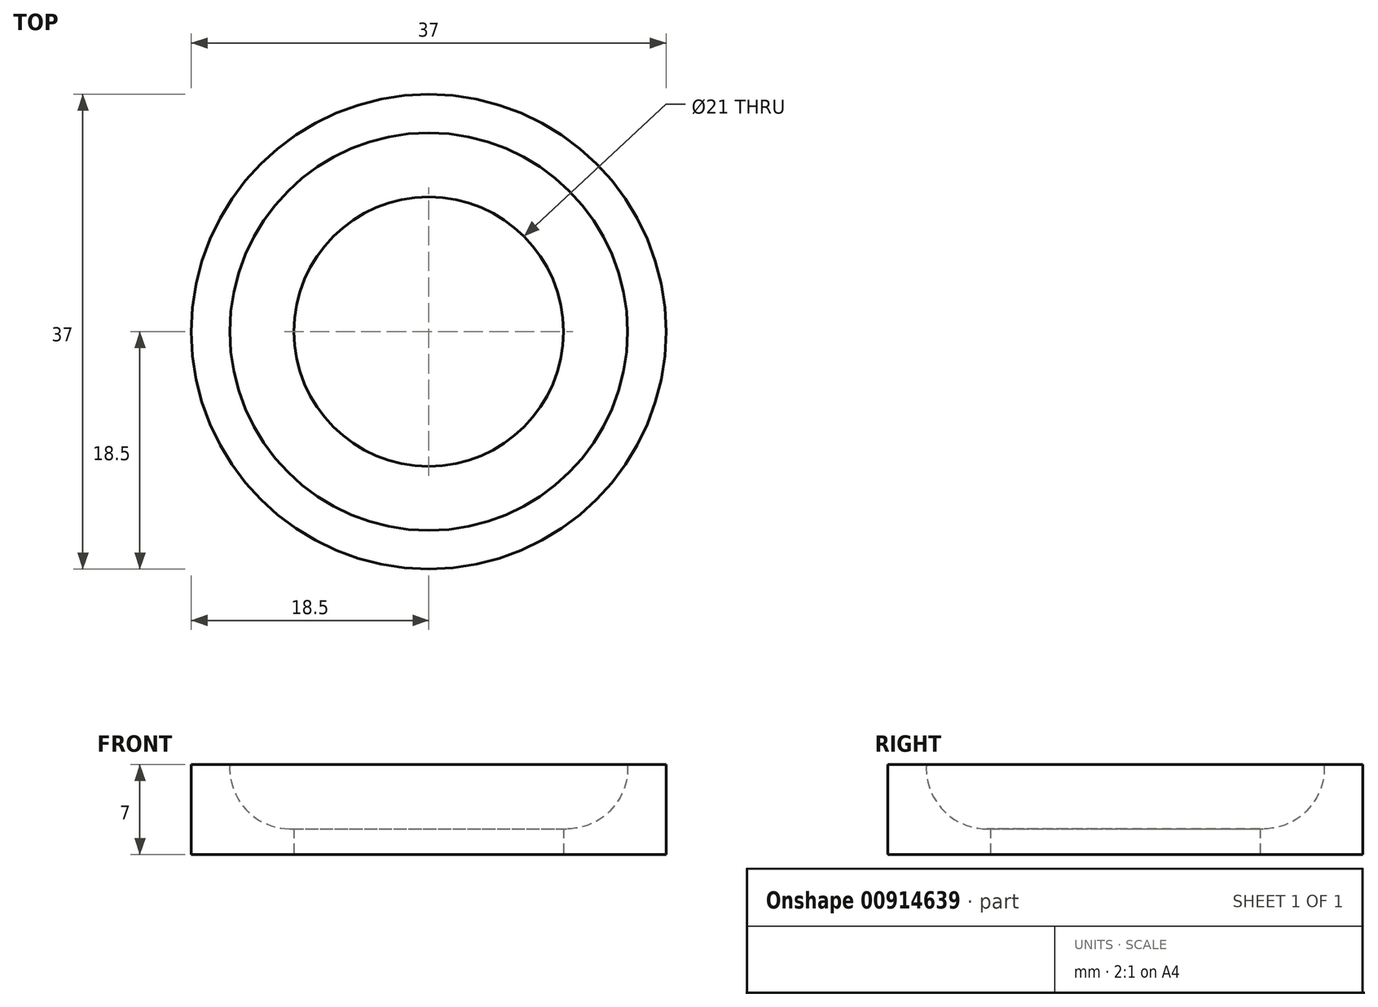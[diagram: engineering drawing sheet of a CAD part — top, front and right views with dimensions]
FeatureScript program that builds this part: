
annotation { "Feature Type Name" : "Feature", "Feature Type Description" : "" }
export const myFeature = defineFeature(function(context is Context, id is Id, definition is map)
    precondition{}
    {
        {
            var Q0;
            Q0=qCreatedBy(makeId("Front.planeOp"),FACE);
            var sketch = newSketch(context, id + "F0", { "sketchPlane" : qUnion([Q0])});
            skLineSegment(sketch, "E0", {"start": v(0, 0) * mm, "end": v(0, 50) * mm, "construction": true});
            skLineSegment(sketch, "E1", {"start": v(10.5, 0) * mm, "end": v(10.5, 2) * mm});
            skLineSegment(sketch, "E2", {"start": v(10.5, 2) * mm, "end": v(10.5, 7) * mm, "construction": true});
            skLineSegment(sketch, "E3", {"start": v(15.5, 7) * mm, "end": v(10.5, 7) * mm, "construction": true});
            skLineSegment(sketch, "E4", {"start": v(15.5, 7) * mm, "end": v(18.5, 7) * mm});
            skLineSegment(sketch, "E5", {"start": v(18.5, 7) * mm, "end": v(18.5, 0) * mm});
            skLineSegment(sketch, "E6", {"start": v(18.5, 0) * mm, "end": v(10.5, 0) * mm});
            skArc(sketch, "E7", {"start": v(10.5, 2) * mm, "mid": v(14.12, 3.38) * mm, "end": v(15.5, 7) * mm});
            skSolve(sketch);
        }
        {
            var Q0;
            Q0 = qSketchRegion(id + "F0", true);
            var Q1;
            Q1=sQuery(id+"F0.wireOp",EDGE,"E0");
            revolve(context, id + "F1", {"surfaceOperationType" : NewSurfaceOperationType.NEW, "entities" : qUnion([Q0]), "axis" : qUnion([Q1]), "revolveType" : RevolveType.FULL});
        }
    });
